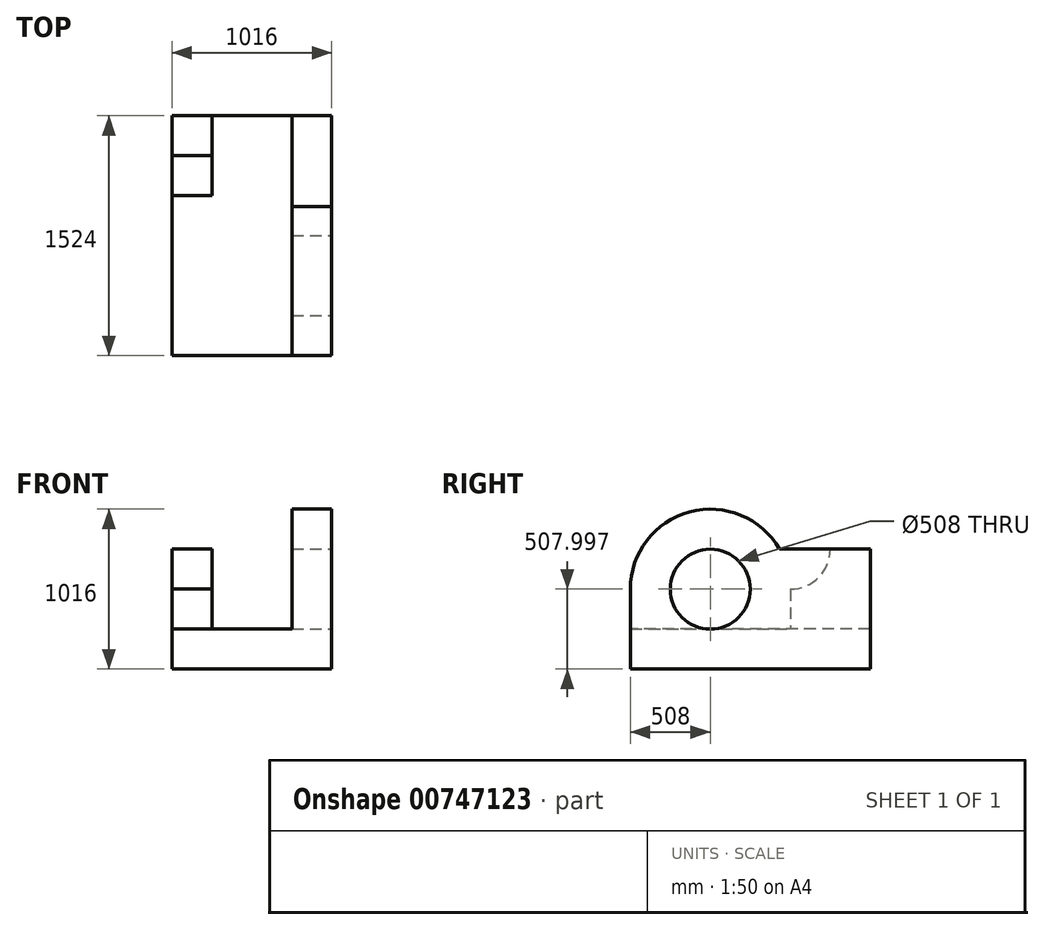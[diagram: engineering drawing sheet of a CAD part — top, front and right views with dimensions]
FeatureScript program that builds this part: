
annotation { "Feature Type Name" : "Feature", "Feature Type Description" : "" }
export const myFeature = defineFeature(function(context is Context, id is Id, definition is map)
    precondition{}
    {
        {
            var Q0;
            Q0=qCreatedBy(makeId("Front.planeOp"),FACE);
            var sketch = newSketch(context, id + "F0", { "sketchPlane" : qUnion([Q0])});
            skLineSegment(sketch, "E0.bottom", {"start": v(-175.22, 143.36) * mm, "end": v(840.78, 143.36) * mm});
            skLineSegment(sketch, "E0.top", {"start": v(-175.22, -110.64) * mm, "end": v(840.78, -110.64) * mm});
            skLineSegment(sketch, "E0.left", {"start": v(-175.22, 143.36) * mm, "end": v(-175.22, -110.64) * mm});
            skLineSegment(sketch, "E0.right", {"start": v(840.78, 143.36) * mm, "end": v(840.78, -110.64) * mm});
            skSolve(sketch);
        }
        {
            var Q0;
            Q0=makeQuery(id+"F0.imprint","IMPRINT",FACE,{"disambiguationData":[TD([[makeQuery(id+"F0.imprint","IMPRINT",EDGE,{"derivedFrom":sQuery(id+"F0.wireOp",EDGE,"E0.bottom")}),-1.0]])]});
            extrude(context, id + "F1", {"entities" : qUnion([Q0]), "depth" : 1524 * mm, "offsetDistance" : 25.4 * mm});
        }
        {
            var Q0;
            Q0=makeQuery(id+"F1.opExtrude","SWEPT_FACE",FACE,{"disambiguationData":[OSD([sQuery(id+"F0.wireOp",EDGE,"E0.bottom")])]});
            var sketch = newSketch(context, id + "F2", { "sketchPlane" : qUnion([Q0])});
            skLineSegment(sketch, "E1", {"start": v(-175.22, 0) * mm, "end": v(78.78, 0) * mm});
            skLineSegment(sketch, "E2", {"start": v(78.78, 0) * mm, "end": v(78.78, -508) * mm});
            skLineSegment(sketch, "E3", {"start": v(78.78, -508) * mm, "end": v(-175.22, -508) * mm});
            skSolve(sketch);
        }
        {
            var Q0;
            {var subQ0=sQuery(id+"F2.wireOp",EDGE,"E1");Q0=makeQuery(id+"F2.imprint","IMPRINT",FACE,{"disambiguationData":[TD([[makeQuery(id+"F2.imprint","IMPRINT",EDGE,{"derivedFrom":subQ0}),-1.0]])]});}
            extrude(context, id + "F3", {"entities" : qUnion([Q0]), "operationType" : NewBodyOperationType.ADD, "depth" : 508 * mm, "offsetDistance" : 25.4 * mm});
        }
        {
            var Q0;
            Q0=makeQuery(id+"F1.opExtrude","SWEPT_FACE",FACE,{"disambiguationData":[OSD([sQuery(id+"F0.wireOp",EDGE,"E0.bottom")])]});
            var sketch = newSketch(context, id + "F4", { "sketchPlane" : qUnion([Q0])});
            skLineSegment(sketch, "E4", {"start": v(840.78, 0) * mm, "end": v(586.78, 0) * mm});
            skLineSegment(sketch, "E5", {"start": v(586.78, 0) * mm, "end": v(586.78, -1524) * mm});
            skSolve(sketch);
        }
        {
            var Q0;
            Q0 = qSketchRegion(id + "F4", true);
            var Q1;
            Q1=makeQuery(id+"F4.imprint","IMPRINT",FACE,{"disambiguationData":[TD([[makeQuery(id+"F4.imprint","IMPRINT",EDGE,{"derivedFrom":sQuery(id+"F4.wireOp",EDGE,"E4")}),-1.0]])]});
            extrude(context, id + "F5", {"entities" : qUnion([Q0, Q1]), "operationType" : NewBodyOperationType.ADD, "depth" : 762 * mm, "offsetDistance" : 25.4 * mm});
        }
        {
            var Q0;
            {var subQ0=sQuery(id+"F0.wireOp",EDGE,"E0.left");Q0=makeQuery(id+"F3.boolean.opBoolean","MERGE",FACE,{"derivedFrom":[makeQuery(id+"F1.opExtrude","SWEPT_FACE",FACE,{"disambiguationData":[OSD([subQ0])]}),makeQuery(id+"F3.opExtrude","SWEPT_FACE",FACE,{"disambiguationData":[OSD([sQuery(id+"F0.wireOp",EDGE,"E0.bottom"),subQ0])]})]});}
            var sketch = newSketch(context, id + "F6", { "sketchPlane" : qUnion([Q0])});
            skLineSegment(sketch, "E6", {"start": v(0, 651.36) * mm, "end": v(254, 651.36) * mm});
            skLineSegment(sketch, "E7", {"start": v(508, 397.36) * mm, "end": v(254, 397.36) * mm});
            skLineSegment(sketch, "E8", {"start": v(254, 651.36) * mm, "end": v(254, 397.36) * mm});
            skCircle(sketch, "E9", {"center": v(508, 651.36) * mm, "radius": 254 * mm});
            skSolve(sketch);
        }
        {
            var Q0;
            {var subQ0=sQuery(id+"F6.wireOp",EDGE,"E9");var subQ1=sQuery(id+"F0.wireOp",EDGE,"E0.left");var subQ2=sQuery(id+"F0.wireOp",EDGE,"E0.bottom");var subQ3=makeQuery(id+"F3.opExtrude","CAP_EDGE",EDGE,{"disambiguationData":[OSD([subQ2,subQ1])],"isStart":false});var subQ4=makeQuery(id+"F6.imprint","INTERSECT",VERTEX,{"derivedFrom":[subQ3,sQuery(id+"F6.wireOp",EDGE,"E6"),sQuery(id+"F6.wireOp",EDGE,"E8"),subQ0]});Q0=makeQuery(id+"F6.imprint","IMPRINT",FACE,{"disambiguationData":[TD([[makeQuery(id+"F6.imprint","IMPRINT",EDGE,{"disambiguationData":[TD([[subQ4,-1.0]])],"derivedFrom":subQ0}),1.0]])]});}
            extrude(context, id + "F7", {"entities" : qUnion([Q0]), "operationType" : NewBodyOperationType.REMOVE, "oppositeDirection" : true, "depth" : 254 * mm, "offsetDistance" : 25.4 * mm});
        }
        {
            var Q0;
            {var subQ0=sQuery(id+"F0.wireOp",EDGE,"E0.right");Q0=makeQuery(id+"F5.boolean.opBoolean","MERGE",FACE,{"derivedFrom":[makeQuery(id+"F1.opExtrude","SWEPT_FACE",FACE,{"disambiguationData":[OSD([subQ0])]}),makeQuery(id+"F5.opExtrude","SWEPT_FACE",FACE,{"disambiguationData":[OSD([sQuery(id+"F0.wireOp",EDGE,"E0.bottom"),subQ0])]})]});}
            var sketch = newSketch(context, id + "F8", { "sketchPlane" : qUnion([Q0])});
            skLineSegment(sketch, "E10", {"start": v(-1524, -110.64) * mm, "end": v(-508, -110.64) * mm});
            skLineSegment(sketch, "E11", {"start": v(-508, -110.64) * mm, "end": v(-508, 905.36) * mm});
            skLineSegment(sketch, "E12", {"start": v(-508, 397.36) * mm, "end": v(-1524, 397.36) * mm});
            skCircle(sketch, "E13", {"center": v(-1016, 397.36) * mm, "radius": 508 * mm});
            skLineSegment(sketch, "E14", {"start": v(-1016, 397.36) * mm, "end": v(-1016, 651.36) * mm});
            skCircle(sketch, "E15", {"center": v(-1016, 397.36) * mm, "radius": 254 * mm});
            skSolve(sketch);
        }
        {
            var Q0;
            {var subQ0=sQuery(id+"F8.wireOp",EDGE,"E14");Q0=makeQuery(id+"F8.imprint","IMPRINT",FACE,{"disambiguationData":[TD([[makeQuery(id+"F8.imprint","IMPRINT",EDGE,{"derivedFrom":subQ0}),1.0]])]});}
            var Q1;
            {var subQ0=sQuery(id+"F8.wireOp",EDGE,"E14");Q1=makeQuery(id+"F8.imprint","IMPRINT",FACE,{"disambiguationData":[TD([[makeQuery(id+"F8.imprint","IMPRINT",EDGE,{"derivedFrom":subQ0}),-1.0]])]});}
            var Q2;
            {var subQ0=sQuery(id+"F8.wireOp",EDGE,"E12");var subQ1=makeQuery(id+"F8.imprint","INTERSECT",VERTEX,{"derivedFrom":[subQ0,sQuery(id+"F8.wireOp",EDGE,"E14")]});Q2=makeQuery(id+"F8.imprint","IMPRINT",FACE,{"disambiguationData":[TD([[makeQuery(id+"F8.imprint","IMPRINT",EDGE,{"disambiguationData":[TD([[subQ1,1.0]])],"derivedFrom":subQ0}),1.0]])]});}
            extrude(context, id + "F9", {"entities" : qUnion([Q0, Q1, Q2]), "operationType" : NewBodyOperationType.REMOVE, "oppositeDirection" : true, "depth" : 254 * mm, "offsetDistance" : 25.4 * mm});
        }
        {
            var Q0;
            {var subQ0=sQuery(id+"F0.wireOp",EDGE,"E0.right");Q0=makeQuery(id+"F5.boolean.opBoolean","MERGE",FACE,{"derivedFrom":[makeQuery(id+"F1.opExtrude","SWEPT_FACE",FACE,{"disambiguationData":[OSD([subQ0])]}),makeQuery(id+"F5.opExtrude","SWEPT_FACE",FACE,{"disambiguationData":[OSD([sQuery(id+"F0.wireOp",EDGE,"E0.bottom"),subQ0])]})]});}
            var sketch = newSketch(context, id + "F10", { "sketchPlane" : qUnion([Q0])});
            skLineSegment(sketch, "E16", {"start": v(-1524, -110.64) * mm, "end": v(-508, -110.64) * mm});
            skLineSegment(sketch, "E17", {"start": v(-508, -110.64) * mm, "end": v(-508, 905.36) * mm});
            skLineSegment(sketch, "E18", {"start": v(-508, 397.36) * mm, "end": v(-1524, 397.36) * mm});
            skCircle(sketch, "E19", {"center": v(-1016, 397.36) * mm, "radius": 508 * mm});
            skLineSegment(sketch, "E20", {"start": v(-508, 397.36) * mm, "end": v(0, 397.36) * mm});
            skLineSegment(sketch, "E21", {"start": v(0, 397.36) * mm, "end": v(0, 651.36) * mm});
            skLineSegment(sketch, "E22", {"start": v(0, 651.36) * mm, "end": v(-576.06, 651.36) * mm});
            skSolve(sketch);
        }
        {
            var Q0;
            {var subQ0=sQuery(id+"F10.wireOp",EDGE,"E18");var subQ1=makeQuery(id+"F9.boolean.opBoolean","COPY",EDGE,{"derivedFrom":makeQuery(id+"F9.opExtrude","CAP_EDGE",EDGE,{"disambiguationData":[OSD([sQuery(id+"F8.wireOp",EDGE,"E15")])],"isStart":true})});var subQ2=makeQuery(id+"F10.imprint","INTERSECT",VERTEX,{"disambiguationData":[OD(0.0)],"derivedFrom":[subQ1,subQ0]});Q0=makeQuery(id+"F10.imprint","IMPRINT",FACE,{"disambiguationData":[TD([[makeQuery(id+"F10.imprint","IMPRINT",EDGE,{"disambiguationData":[TD([[subQ2,-1.0]])],"derivedFrom":subQ0}),1.0]])]});}
            var Q1;
            {var subQ0=sQuery(id+"F10.wireOp",EDGE,"E18");var subQ1=makeQuery(id+"F9.boolean.opBoolean","COPY",EDGE,{"derivedFrom":makeQuery(id+"F9.opExtrude","CAP_EDGE",EDGE,{"disambiguationData":[OSD([sQuery(id+"F8.wireOp",EDGE,"E15")])],"isStart":true})});var subQ2=makeQuery(id+"F10.imprint","INTERSECT",VERTEX,{"disambiguationData":[OD(0.0)],"derivedFrom":[subQ1,subQ0]});Q1=makeQuery(id+"F10.imprint","IMPRINT",FACE,{"disambiguationData":[TD([[makeQuery(id+"F10.imprint","IMPRINT",EDGE,{"disambiguationData":[TD([[subQ2,-1.0]])],"derivedFrom":subQ0}),-1.0]])]});}
            var Q2;
            {var subQ0=sQuery(id+"F10.wireOp",EDGE,"E19");var subQ1=sQuery(id+"F0.wireOp",EDGE,"E0.right");var subQ2=sQuery(id+"F0.wireOp",EDGE,"E0.bottom");var subQ5=makeQuery(id+"F5.opExtrude","CAP_EDGE",EDGE,{"disambiguationData":[OSD([subQ2,subQ1])],"isStart":false});var subQ6=makeQuery(id+"F10.imprint","INTERSECT",VERTEX,{"derivedFrom":[subQ5,subQ0]});Q2=makeQuery(id+"F10.imprint","IMPRINT",FACE,{"disambiguationData":[TD([[makeQuery(id+"F10.imprint","IMPRINT",EDGE,{"disambiguationData":[TD([[subQ6,-1.0]])],"derivedFrom":subQ0}),-1.0]])]});}
            var Q3;
            {var subQ3=sQuery(id+"F10.wireOp",EDGE,"E22");var subQ5=sQuery(id+"F10.wireOp",EDGE,"E19");var subQ6=makeQuery(id+"F10.imprint","INTERSECT",VERTEX,{"derivedFrom":[subQ5,subQ3]});Q3=makeQuery(id+"F10.imprint","IMPRINT",FACE,{"disambiguationData":[TD([[makeQuery(id+"F10.imprint","IMPRINT",EDGE,{"disambiguationData":[TD([[subQ6,1.0]])],"derivedFrom":subQ3}),-1.0]])]});}
            var Q4;
            {var subQ0=sQuery(id+"F10.wireOp",EDGE,"E17");var subQ5=sQuery(id+"F10.wireOp",EDGE,"E22");var subQ6=makeQuery(id+"F10.imprint","INTERSECT",VERTEX,{"derivedFrom":[subQ0,subQ5]});Q4=makeQuery(id+"F10.imprint","IMPRINT",FACE,{"disambiguationData":[TD([[makeQuery(id+"F10.imprint","IMPRINT",EDGE,{"disambiguationData":[TD([[subQ6,-1.0]])],"derivedFrom":subQ0}),-1.0]])]});}
            extrude(context, id + "F11", {"entities" : qUnion([Q0, Q1, Q2, Q3, Q4]), "operationType" : NewBodyOperationType.REMOVE, "oppositeDirection" : true, "depth" : 254 * mm, "offsetDistance" : 25.4 * mm});
        }
    });
